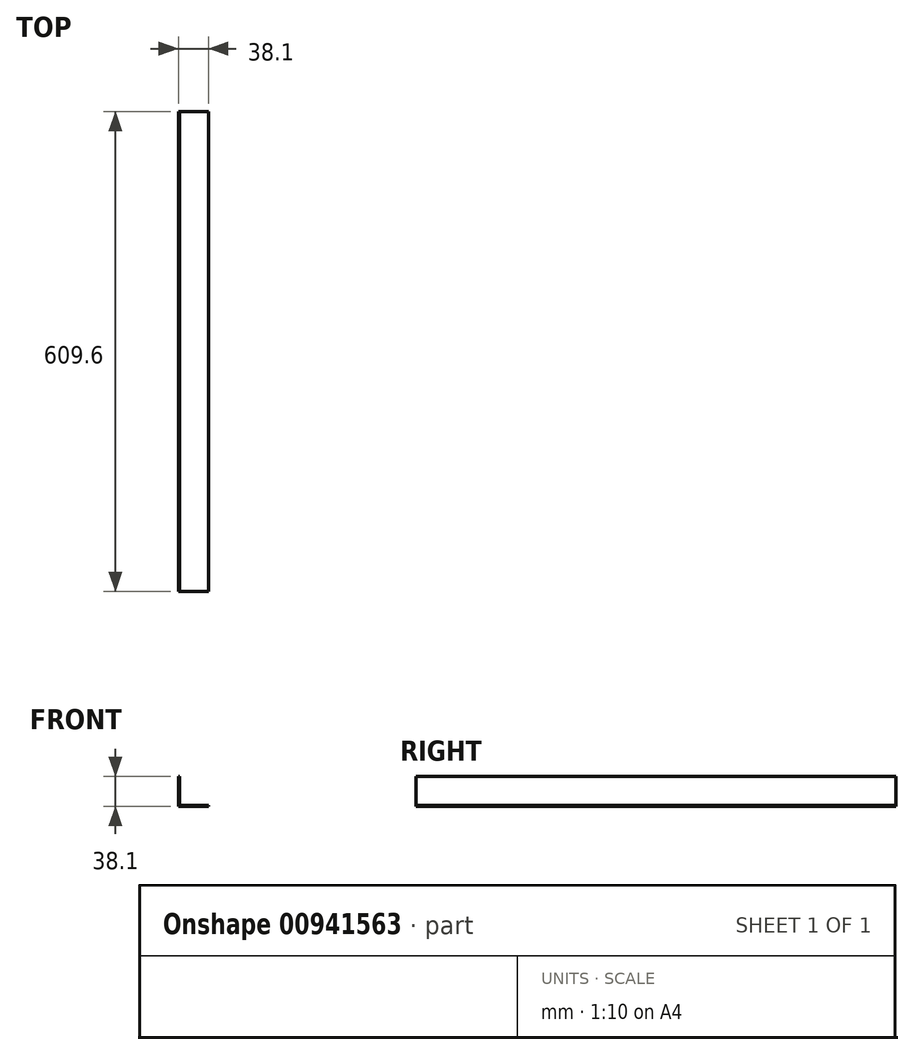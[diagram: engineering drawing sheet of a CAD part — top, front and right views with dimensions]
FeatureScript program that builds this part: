
annotation { "Feature Type Name" : "Feature", "Feature Type Description" : "" }
export const myFeature = defineFeature(function(context is Context, id is Id, definition is map)
    precondition{}
    {
        {
            var Q0;
            Q0=qCreatedBy(makeId("Front.planeOp"),FACE);
            var sketch = newSketch(context, id + "F0", { "sketchPlane" : qUnion([Q0])});
            skLineSegment(sketch, "E0", {"start": v(0, 0) * mm, "end": v(0, 38.1) * mm});
            skLineSegment(sketch, "E1", {"start": v(0, 0) * mm, "end": v(38.1, 0) * mm});
            skLineSegment(sketch, "E2.0", {"start": v(1.59, 1.59) * mm, "end": v(1.59, 38.1) * mm});
            skLineSegment(sketch, "E3.0", {"start": v(1.59, 1.59) * mm, "end": v(38.1, 1.59) * mm});
            skLineSegment(sketch, "E4", {"start": v(0, 38.1) * mm, "end": v(1.59, 38.1) * mm});
            skLineSegment(sketch, "E5", {"start": v(38.1, 1.59) * mm, "end": v(38.1, 0) * mm});
            skSolve(sketch);
        }
        {
            var Q0;
            Q0=qSketchRegion(id+"F0",true);
            extrude(context, id + "F1", {"entities" : qUnion([Q0]), "depth" : 609.6 * mm, "offsetDistance" : 25.4 * mm});
        }
    });
